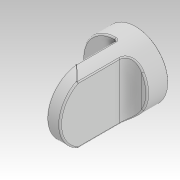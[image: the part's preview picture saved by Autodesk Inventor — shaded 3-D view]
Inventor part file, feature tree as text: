
AUTODESK INVENTOR PART (.ipt)
format: ipt  version: 2020 (Build 240168000, 168)  size: 433,664 bytes
history: native  units: mm
features: extrude x16, sketch x16, fillet x4, projected_geometry x4, plane x1, chamfer x1
ambient origin geometry x8: Origin, YZ Plane, XZ Plane, XY Plane, X Axis, Y Axis, Z Axis, Center Point
bodies: Solid1 (feature_tree)
feature tree (42):
  extrude  "Extrusion1"  Depth=90.0mm
  extrude  "Extrusion2"  Depth=53.0mm
  extrude  "Extrusion3"  Depth=29.0mm TaperAngle=0.0deg
  extrude  "Extrusion4"  Depth=42.0mm
  extrude  "Extrusion5"  Depth=27.0mm
  fillet  "Fillet2"  Radius=59.0mm
  extrude  "Extrusion6"  Depth=3.5mm TaperAngle=0.0deg
  extrude  "Extrusion7"  Depth=10.0mm TaperAngle=0.0deg
  extrude  "Extrusion8"  Depth=7.0mm TaperAngle=0.0deg
  plane  "Work Plane1"
  extrude  "Extrusion9"  Depth=13.0mm
  extrude  "Extrusion10"  Depth=7.5mm TaperAngle=0.0deg
  extrude  "Extrusion11"  Depth=7.5mm
  extrude  "Extrusion12"  Depth=7.5mm TaperAngle=0.0deg
  fillet  "Fillet3"  Radius=7.5mm
  fillet  "Fillet4"  Radius=7.5mm
  extrude  "Extrusion13"  Depth=2.0mm
  extrude  "Extrusion14"  Depth=10.0mm TaperAngle=0.0deg
  fillet  "Fillet5"  Radius=3.0mm
  chamfer  "Chamfer2"  Distance=2.0mm Angle=45.0deg
  extrude  "Extrusion15"  Depth=10.0mm
  extrude  "Extrusion16"  Depth=10.0mm
  sketch  "Sketch1"  dims[d0=50.0mm d1=90.0mm]
  sketch  "Sketch2"  dims[d2=19.0mm d3=0.0mm d4=53.0mm]
  sketch  "Sketch3"  dims[d5=90.0mm d7=29.0mm d8=0.0mm]
  sketch  "Sketch4"  dims[d9=12.5mm d10=42.0mm]
  sketch  "Sketch5"  dims[d11=27.0mm d12=0.0mm d15=86.0mm d16=59.0mm]
  projected_geometry  "Projected Loop1"
  projected_geometry  "Projected Loop2"
  sketch  "Sketch6"  dims[d17=3.5mm d18=0.0mm d19=25.0mm d20=0.0mm]
  sketch  "Sketch7"  dims[d21=15.0mm d22=10.0mm d23=0.0mm]
  sketch  "Sketch8"  dims[d24=34.9mm d25=7.0mm d26=0.0mm]
  sketch  "Sketch9"  dims[d27=5.1mm d28=13.0mm]
  sketch  "Sketch10"  dims[d29=60.0mm d31=360.0deg d33=7.5mm d34=0.0mm]
  sketch  "Sketch11"  dims[d35=-10.0mm d36=7.5mm]
  sketch  "Sketch12"  dims[d37=7.5mm d38=0.0mm d39=7.5mm d40=0.0mm d41=7.5mm d42=0.0mm d43=7.5mm d44=0.0mm]
  sketch  "Sketch13"  dims[d45=5.0mm d46=2.0mm]
  projected_geometry  "Projected Loop3"
  sketch  "Sketch14"  dims[d50=10.0mm d51=0.0mm d52=10.0mm d53=0.0mm d54=3.0mm]
  projected_geometry  "Projected Loop4"
  sketch  "Sketch15"  dims[d55=2.0mm d56=0.5mm d57=2.0mm d58=45.0deg]
  sketch  "Sketch16"  dims[d59=3.0mm d60=0.0mm d61=50.0mm d62=5.0mm d63=10.0mm d64=0.0mm]
